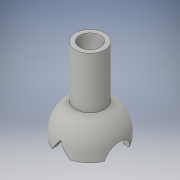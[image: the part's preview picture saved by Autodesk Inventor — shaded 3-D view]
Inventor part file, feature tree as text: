
AUTODESK INVENTOR PART (.ipt)
format: ipt  version: 2016 (Build 200138000, 138)  size: 167,424 bytes
history: native  units: in
note: dims shown in document units (in); Inventor stores cm internally (conversion verified against a paired STEP export)
features: sketch x4, extrude x3, revolve x1
ambient origin geometry x8: Origin, YZ Plane, XZ Plane, XY Plane, X Axis, Y Axis, Z Axis, Center Point
bodies: Solid1 (feature_tree)
feature tree (8):
  revolve  "Revolution1"  [1 undecoded]
  extrude  "Extrusion1"  Depth=0.246in
  extrude  "Extrusion2"  Depth=0.3in TaperAngle=0.0deg
  extrude  "Extrusion3"  Depth=4.0in TaperAngle=0.0deg
  sketch  "Sketch1"  dims[d0=0.6in d1=0.06in]
  sketch  "Sketch2"  dims[d2=90.0deg d3=0.246in]
  sketch  "Sketch3"  dims[d4=0.3in d5=0.0in d6=4.0in d7=0.0in]
  sketch  "Sketch4"  dims[d8=0.8727in d9=4.0in d10=0.0in]
note: 1 required parameter value undecoded (feature->parameter linkage not recoverable at this tier; creation-order binding heuristic only, values carry confidence <= 0.55)
